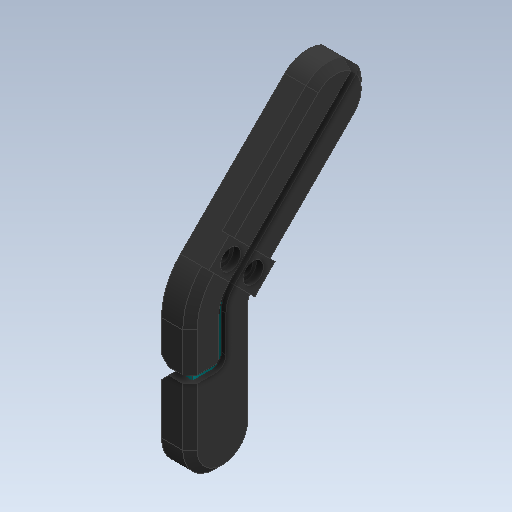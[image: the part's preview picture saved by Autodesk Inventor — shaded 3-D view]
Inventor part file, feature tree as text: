
AUTODESK INVENTOR PART (.ipt)
format: ipt  version: 2020 (Build 240168000, 168)  size: 405,504 bytes
history: native  units: in
note: dims shown in document units (in); Inventor stores cm internally (conversion verified against a paired STEP export)
features: sketch x30, other x7, plane x4
ambient origin geometry x8: Origin, YZ Plane, XZ Plane, XY Plane, X Axis, Y Axis, Z Axis, Center Point
bodies: Solid2 (feature_tree), Solid3 (feature_tree), Solid1 (feature_tree), Solid4 (feature_tree)
feature tree (41):
  other  "PatellaTop.ipt"
  other  "Solid1::PatellaTop.ipt"
  other  "Solid4::PatellaTop.ipt"
  other  "Solid5::PatellaTop.ipt"
  other  "Solid2::PatellaTop.ipt"
  other  "Solid3::PatellaTop.ipt"
  other  "TaggingFeature1"
  sketch  "Sketch1"  dims[d0=0.3937in]
  sketch  "Sketch2"
  sketch  "Sketch3"
  sketch  "Sketch4"
  sketch  "Sketch5"
  sketch  "Sketch12"
  sketch  "Sketch14"
  sketch  "Sketch15"
  sketch  "Sketch16"
  sketch  "Sketch17"
  sketch  "Sketch19"
  sketch  "Sketch22"
  sketch  "Sketch23"
  sketch  "Sketch24"
  sketch  "Sketch25"
  sketch  "Sketch26"
  sketch  "Sketch27"
  sketch  "Sketch28"
  sketch  "Sketch29"
  sketch  "Sketch30"
  sketch  "Sketch31"
  sketch  "Sketch32"
  sketch  "Sketch33"
  sketch  "Sketch39"
  sketch  "Sketch40"
  sketch  "Sketch44"
  sketch  "Sketch45"
  sketch  "Sketch46"
  sketch  "Sketch48"
  sketch  "Sketch49"
  plane  "Work Plane1"
  plane  "Work Plane2"
  plane  "Work Plane3"
  plane  "Work Plane4"
